# Revit family: Cellular Beam with un-Equidistant End Holes
name_source: partatom
category: Structural Framing
revit_build: Autodesk Revit 2017 (Build: 20161117_1200(x64)
units: mm (PartAtom-declared; Revit-internal decimal feet)

## family parameters
Always export as geometry = No
Always vertical = Yes
Cut with Voids When Loaded = No
Material for Model Behavior = Steel
Section Shape = Not Defined
Shared = No
Show family pre-cut in plan views = Yes
Structural Framing Length Roundoff = 1 mm

## types (2) — shared parameters
S1 = 409 mm
Structural Material = Metal - Steel - S 275
tf1 = 9 mm  [stored 0.0295276 ft]
tw1 = 6 mm  [stored 0.019685 ft]
zero-valued in all types: Setback Left, Setback Right

## per-type parameters (varying)
| type | Do | Name1 | Name2 | S | W1 | W2 | bf1 | bf2 | d | d1 | d2 | dt1 | dt2 | e | h1 | h2 | k1 | k2 | r1 | r2 | tf2 | tw2 |
| LB457x28 | 409 mm | UB305x102x28 | UB305x102x28 | 614 mm | 27.6 | 27.6 | 102 mm | 102 mm | 486 mm | 309 mm | 309 mm | 38 mm | 38 mm | 205 mm  [stored 0.672572 ft] | 205 mm  [stored 0.672572 ft] | 205 mm  [stored 0.672572 ft] | 17 mm | 17 mm | 8 mm  [stored 0.0262467 ft] | 8 mm  [stored 0.0262467 ft] | 9 mm  [stored 0.0295276 ft] | 6 mm  [stored 0.019685 ft] |
| LB533x33/39 | 360 mm  [stored 1.1811 ft] | UB356x127x33 | UB356x127x39 | 626 mm | 32.4 | 38.3 | 125 mm  [stored 0.410105 ft] | 126 mm  [stored 0.413386 ft] | 472 mm | 349 mm | 353 mm | 55 mm  [stored 0.180446 ft] | 57 mm | 266 mm | 180 mm  [stored 0.590551 ft] | 180 mm  [stored 0.590551 ft] | 19 mm | 21 mm | 10 mm  [stored 0.0328084 ft] | 10 mm  [stored 0.0328084 ft] | 11 mm | 7 mm  [stored 0.0229659 ft] |

note: [stored X ft] marks values corroborated as IEEE doubles in the binary element streams (Revit-internal decimal feet)

## geometry (parser evidence)
native form markers: Blend x4, Sweep x6
no freeform markers — native parametric forms only
